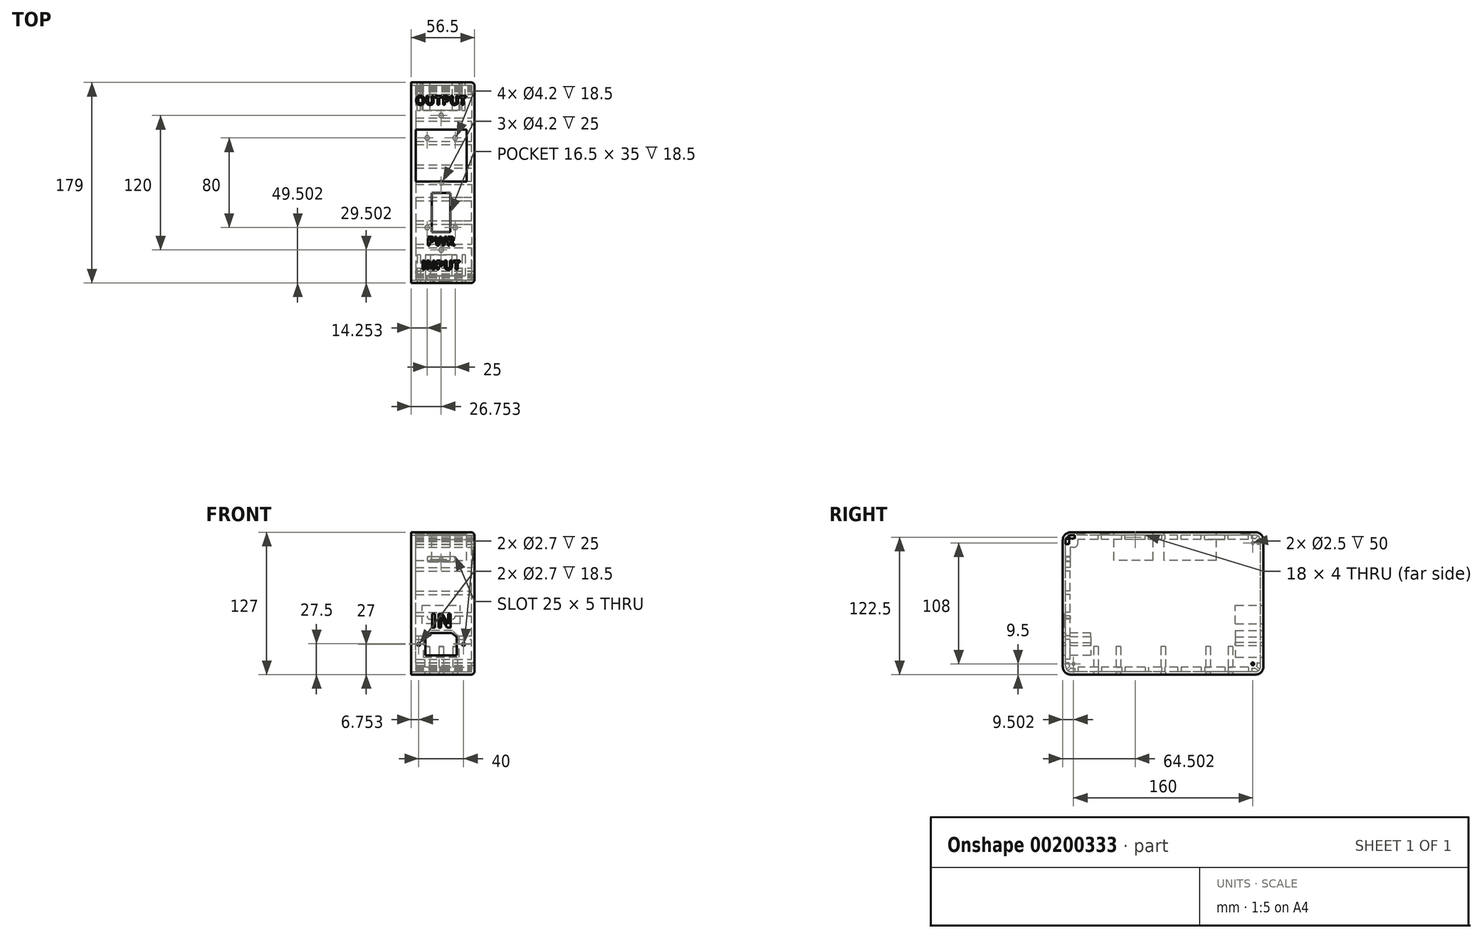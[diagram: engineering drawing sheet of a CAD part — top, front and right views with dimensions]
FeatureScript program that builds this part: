
annotation { "Feature Type Name" : "Feature", "Feature Type Description" : "" }
export const myFeature = defineFeature(function(context is Context, id is Id, definition is map)
    precondition{}
    {
        {
            var Q0;
            Q0=qCreatedBy(makeId("Top.planeOp"),FACE);
            var sketch = newSketch(context, id + "F0", { "sketchPlane" : qUnion([Q0])});
            skLineSegment(sketch, "E0.bottom", {"start": v(-53, 83.4) * mm, "end": v(59, 83.4) * mm});
            skLineSegment(sketch, "E0.top", {"start": v(-53, -90.6) * mm, "end": v(59, -90.6) * mm});
            skLineSegment(sketch, "E0.left", {"start": v(-58, 78.4) * mm, "end": v(-58, -85.6) * mm});
            skLineSegment(sketch, "E0.right", {"start": v(64, 78.4) * mm, "end": v(64, -85.6) * mm});
            skLineSegment(sketch, "E1.1", {"start": v(-54, 72.4) * mm, "end": v(-54, -79.6) * mm});
            skLineSegment(sketch, "E1.2", {"start": v(-47, -86.6) * mm, "end": v(53, -86.6) * mm});
            skLineSegment(sketch, "E1.3", {"start": v(60, 72.4) * mm, "end": v(60, -79.6) * mm});
            skLineSegment(sketch, "E2.bottom", {"start": v(-29, 49.4) * mm, "end": v(16, 49.4) * mm, "construction": true});
            skLineSegment(sketch, "E2.top", {"start": v(-29, 3.4) * mm, "end": v(16, 3.4) * mm, "construction": true});
            skLineSegment(sketch, "E2.left", {"start": v(-29, 49.4) * mm, "end": v(-29, 3.4) * mm, "construction": true});
            skLineSegment(sketch, "E2.right", {"start": v(16, 49.4) * mm, "end": v(16, 3.4) * mm, "construction": true});
            skLineSegment(sketch, "E3.0", {"start": v(-60.5, 78.9) * mm, "end": v(-60.5, -86.1) * mm});
            skLineSegment(sketch, "E3.1", {"start": v(-53.5, 85.9) * mm, "end": v(59.5, 85.9) * mm});
            skLineSegment(sketch, "E3.2", {"start": v(66.5, 78.9) * mm, "end": v(66.5, -86.1) * mm});
            skLineSegment(sketch, "E3.3", {"start": v(-53.5, -93.1) * mm, "end": v(59.5, -93.1) * mm});
            skLineSegment(sketch, "E4", {"start": v(66, 49.4) * mm, "end": v(98.5, 49.4) * mm, "construction": true});
            skLineSegment(sketch, "E5", {"start": v(98.5, 49.4) * mm, "end": v(98.5, 32.4) * mm, "construction": true});
            skLineSegment(sketch, "E6", {"start": v(98.5, 32.4) * mm, "end": v(92.24, 25.4) * mm, "construction": true});
            skLineSegment(sketch, "E7", {"start": v(92.24, 25.4) * mm, "end": v(72.24, 25.4) * mm, "construction": true});
            skLineSegment(sketch, "E8", {"start": v(72.24, 25.4) * mm, "end": v(66, 32.4) * mm, "construction": true});
            skLineSegment(sketch, "E9", {"start": v(66, 32.4) * mm, "end": v(66, 49.4) * mm, "construction": true});
            skLineSegment(sketch, "E10", {"start": v(82.24, 25.4) * mm, "end": v(82.24, 49.4) * mm, "construction": true});
            skLineSegment(sketch, "E11.bottom", {"start": v(65.5, 3.4) * mm, "end": v(99, 3.4) * mm, "construction": true});
            skLineSegment(sketch, "E11.top", {"start": v(65.5, 19.4) * mm, "end": v(99, 19.4) * mm, "construction": true});
            skLineSegment(sketch, "E11.left", {"start": v(65.5, 3.4) * mm, "end": v(65.5, 19.4) * mm, "construction": true});
            skLineSegment(sketch, "E11.right", {"start": v(99, 3.4) * mm, "end": v(99, 19.4) * mm, "construction": true});
            skLineSegment(sketch, "E12", {"start": v(82.24, 19.4) * mm, "end": v(82.24, 25.4) * mm, "construction": true});
            skLineSegment(sketch, "E13.bottom", {"start": v(26, 9.4) * mm, "end": v(41, 9.4) * mm, "construction": true});
            skLineSegment(sketch, "E13.top", {"start": v(26, 43.4) * mm, "end": v(41, 43.4) * mm, "construction": true});
            skLineSegment(sketch, "E13.left", {"start": v(26, 9.4) * mm, "end": v(26, 43.4) * mm, "construction": true});
            skLineSegment(sketch, "E13.right", {"start": v(41, 9.4) * mm, "end": v(41, 43.4) * mm, "construction": true});
            skLineSegment(sketch, "E14", {"start": v(26, 26.4) * mm, "end": v(16, 26.4) * mm, "construction": true});
            skPoint(sketch, "E15.visualSharp", {"position": v(-54, 79.4) * mm});
            skArc(sketch, "E15.filletArc", {"start": v(-51, 79.28) * mm, "mid": v(-52.84, 78.23) * mm, "end": v(-53.88, 76.4) * mm});
            skPoint(sketch, "E16.visualSharp", {"position": v(60, 79.4) * mm});
            skPoint(sketch, "E17.visualSharp", {"position": v(-54, -86.6) * mm});
            skArc(sketch, "E17.filletArc", {"start": v(-53.88, -83.6) * mm, "mid": v(-52.84, -85.43) * mm, "end": v(-51, -86.47) * mm});
            skPoint(sketch, "E18.visualSharp", {"position": v(60, -86.6) * mm});
            skPoint(sketch, "E19.visualSharp", {"position": v(64, -90.6) * mm});
            skArc(sketch, "E19.filletArc", {"start": v(59, -90.6) * mm, "mid": v(62.53, -89.13) * mm, "end": v(64, -85.6) * mm});
            skPoint(sketch, "E20.visualSharp", {"position": v(-58, -90.6) * mm});
            skArc(sketch, "E20.filletArc", {"start": v(-58, -85.6) * mm, "mid": v(-56.54, -89.13) * mm, "end": v(-53, -90.6) * mm});
            skPoint(sketch, "E21.visualSharp", {"position": v(64, 83.4) * mm});
            skArc(sketch, "E21.filletArc", {"start": v(64, 78.4) * mm, "mid": v(62.53, 81.94) * mm, "end": v(59, 83.4) * mm});
            skPoint(sketch, "E22.visualSharp", {"position": v(-58, 83.4) * mm});
            skArc(sketch, "E22.filletArc", {"start": v(-53, 83.4) * mm, "mid": v(-56.54, 81.94) * mm, "end": v(-58, 78.4) * mm});
            skPoint(sketch, "E23.visualSharp", {"position": v(-60.5, 85.9) * mm});
            skArc(sketch, "E23.filletArc", {"start": v(-53.5, 85.9) * mm, "mid": v(-58.46, 83.85) * mm, "end": v(-60.5, 78.9) * mm});
            skPoint(sketch, "E24.visualSharp", {"position": v(66.5, 85.9) * mm});
            skArc(sketch, "E24.filletArc", {"start": v(66.5, 78.9) * mm, "mid": v(64.44, 83.85) * mm, "end": v(59.5, 85.9) * mm});
            skPoint(sketch, "E25.visualSharp", {"position": v(66.5, -93.1) * mm});
            skArc(sketch, "E25.filletArc", {"start": v(59.5, -93.1) * mm, "mid": v(64.44, -91.05) * mm, "end": v(66.5, -86.1) * mm});
            skPoint(sketch, "E26.visualSharp", {"position": v(-60.5, -93.1) * mm});
            skArc(sketch, "E26.filletArc", {"start": v(-60.5, -86.1) * mm, "mid": v(-58.46, -91.05) * mm, "end": v(-53.5, -93.1) * mm});
            skLineSegment(sketch, "E27", {"start": v(-50, 80.28) * mm, "end": v(-50, 83.4) * mm});
            skLineSegment(sketch, "E28", {"start": v(-52.95, 78.1) * mm, "end": v(-56.54, 81.94) * mm, "construction": true});
            skLineSegment(sketch, "E29.0", {"start": v(-53.15, 79.78) * mm, "end": v(-55.77, 82.57) * mm});
            skLineSegment(sketch, "E30.0", {"start": v(-54.52, 78.32) * mm, "end": v(-57.18, 81.16) * mm});
            skLineSegment(sketch, "E31.0", {"start": v(-47, 76.4) * mm, "end": v(-47, 83.4) * mm});
            skLineSegment(sketch, "E32.0", {"start": v(-29, 79.4) * mm, "end": v(-29, 83.4) * mm});
            skLineSegment(sketch, "E33.0", {"start": v(-26, 79.4) * mm, "end": v(-26, 83.4) * mm});
            skLineSegment(sketch, "E34.0", {"start": v(-8, 79.4) * mm, "end": v(-8, 83.4) * mm});
            skLineSegment(sketch, "E35.0", {"start": v(-5, 79.4) * mm, "end": v(-5, 83.4) * mm});
            skLineSegment(sketch, "E36", {"start": v(3, 85.9) * mm, "end": v(3, 79.4) * mm, "construction": true});
            skLineSegment(sketch, "E37", {"start": v(-54.88, 75.4) * mm, "end": v(-58, 75.4) * mm});
            skLineSegment(sketch, "E38.0", {"start": v(-51, 72.4) * mm, "end": v(-58, 72.4) * mm});
            skLineSegment(sketch, "E39.0", {"start": v(-54, 54.4) * mm, "end": v(-58, 54.4) * mm});
            skLineSegment(sketch, "E40.0", {"start": v(-54, 51.4) * mm, "end": v(-58, 51.4) * mm});
            skLineSegment(sketch, "E41.0", {"start": v(-54, 33.4) * mm, "end": v(-58, 33.4) * mm});
            skLineSegment(sketch, "E42.0", {"start": v(-54, 30.4) * mm, "end": v(-58, 30.4) * mm});
            skLineSegment(sketch, "E43.0", {"start": v(-54, 12.4) * mm, "end": v(-58, 12.4) * mm});
            skLineSegment(sketch, "E44.0", {"start": v(-54, 9.4) * mm, "end": v(-58, 9.4) * mm});
            skLineSegment(sketch, "E45", {"start": v(-60.5, -3.6) * mm, "end": v(-54, -3.6) * mm, "construction": true});
            skLineSegment(sketch, "E46.0", {"start": v(-58, -2.1) * mm, "end": v(-54, -2.1) * mm});
            skLineSegment(sketch, "E47.MirrorCS", {"start": v(-58, -5.1) * mm, "end": v(-54, -5.1) * mm});
            skLineSegment(sketch, "E48.MirrorCS", {"start": v(-54, -16.6) * mm, "end": v(-58, -16.6) * mm});
            skLineSegment(sketch, "E49.MirrorCS", {"start": v(-54, -19.6) * mm, "end": v(-58, -19.6) * mm});
            skLineSegment(sketch, "E50.MirrorCS", {"start": v(-54, -37.6) * mm, "end": v(-58, -37.6) * mm});
            skLineSegment(sketch, "E51.MirrorCS", {"start": v(-54, -40.6) * mm, "end": v(-58, -40.6) * mm});
            skLineSegment(sketch, "E52.MirrorCS", {"start": v(-51, -79.6) * mm, "end": v(-58, -79.6) * mm});
            skLineSegment(sketch, "E53.MirrorCS", {"start": v(-54.88, -82.6) * mm, "end": v(-58, -82.6) * mm});
            skLineSegment(sketch, "E54.MirrorCS", {"start": v(-54.52, -85.51) * mm, "end": v(-57.18, -88.35) * mm});
            skLineSegment(sketch, "E55.MirrorCS", {"start": v(-53.15, -86.98) * mm, "end": v(-55.77, -89.77) * mm});
            skLineSegment(sketch, "E56.MirrorCS", {"start": v(-50, -87.47) * mm, "end": v(-50, -90.6) * mm});
            skLineSegment(sketch, "E57.MirrorCS", {"start": v(-47, -83.6) * mm, "end": v(-47, -90.6) * mm});
            skLineSegment(sketch, "E58.MirrorCS", {"start": v(-29, -86.6) * mm, "end": v(-29, -90.6) * mm});
            skLineSegment(sketch, "E59.MirrorCS", {"start": v(-26, -86.6) * mm, "end": v(-26, -90.6) * mm});
            skLineSegment(sketch, "E60.MirrorCS", {"start": v(-8, -86.6) * mm, "end": v(-8, -90.6) * mm});
            skLineSegment(sketch, "E61.MirrorCS", {"start": v(-5, -86.6) * mm, "end": v(-5, -90.6) * mm});
            skLineSegment(sketch, "E62.MirrorCS", {"start": v(-54, -61.6) * mm, "end": v(-58, -61.6) * mm});
            skLineSegment(sketch, "E63.MirrorCS", {"start": v(-54, -58.6) * mm, "end": v(-58, -58.6) * mm});
            skLineSegment(sketch, "E64.MirrorCS", {"start": v(11, 79.4) * mm, "end": v(11, 83.4) * mm});
            skLineSegment(sketch, "E65.MirrorCS", {"start": v(14, 79.4) * mm, "end": v(14, 83.4) * mm});
            skLineSegment(sketch, "E66.MirrorCS", {"start": v(32, 79.4) * mm, "end": v(32, 83.4) * mm});
            skLineSegment(sketch, "E67.MirrorCS", {"start": v(35, 79.4) * mm, "end": v(35, 83.4) * mm});
            skLineSegment(sketch, "E68.MirrorCS", {"start": v(53, 76.4) * mm, "end": v(53, 83.4) * mm});
            skLineSegment(sketch, "E69.MirrorCS", {"start": v(56, 79.4) * mm, "end": v(56, 83.4) * mm});
            skLineSegment(sketch, "E70.MirrorCS", {"start": v(59.13, 79.78) * mm, "end": v(61.75, 82.57) * mm});
            skLineSegment(sketch, "E71.MirrorCS", {"start": v(60.5, 78.32) * mm, "end": v(63.17, 81.16) * mm});
            skLineSegment(sketch, "E72.MirrorCS", {"start": v(60, 75.4) * mm, "end": v(64, 75.4) * mm});
            skLineSegment(sketch, "E73.MirrorCS", {"start": v(57, 72.4) * mm, "end": v(64, 72.4) * mm});
            skLineSegment(sketch, "E74.MirrorCS", {"start": v(60, 54.4) * mm, "end": v(64, 54.4) * mm});
            skLineSegment(sketch, "E75.MirrorCS", {"start": v(60, 51.4) * mm, "end": v(64, 51.4) * mm});
            skLineSegment(sketch, "E76.MirrorCS", {"start": v(60, 33.4) * mm, "end": v(64, 33.4) * mm});
            skLineSegment(sketch, "E77.MirrorCS", {"start": v(60, 30.4) * mm, "end": v(64, 30.4) * mm});
            skLineSegment(sketch, "E78.MirrorCS", {"start": v(60, 12.4) * mm, "end": v(64, 12.4) * mm});
            skLineSegment(sketch, "E79.MirrorCS", {"start": v(60, 9.4) * mm, "end": v(64, 9.4) * mm});
            skLineSegment(sketch, "E80.MirrorCS", {"start": v(64, -2.1) * mm, "end": v(60, -2.1) * mm});
            skLineSegment(sketch, "E81.MirrorCS", {"start": v(64, -5.1) * mm, "end": v(60, -5.1) * mm});
            skLineSegment(sketch, "E82.MirrorCS", {"start": v(60, -16.6) * mm, "end": v(64, -16.6) * mm});
            skLineSegment(sketch, "E83.MirrorCS", {"start": v(60, -19.6) * mm, "end": v(64, -19.6) * mm});
            skLineSegment(sketch, "E84.MirrorCS", {"start": v(60, -37.6) * mm, "end": v(64, -37.6) * mm});
            skLineSegment(sketch, "E85.MirrorCS", {"start": v(60, -40.6) * mm, "end": v(64, -40.6) * mm});
            skLineSegment(sketch, "E86.MirrorCS", {"start": v(60, -58.6) * mm, "end": v(64, -58.6) * mm});
            skLineSegment(sketch, "E87.MirrorCS", {"start": v(60, -61.6) * mm, "end": v(64, -61.6) * mm});
            skLineSegment(sketch, "E88.MirrorCS", {"start": v(57, -79.6) * mm, "end": v(64, -79.6) * mm});
            skLineSegment(sketch, "E89.MirrorCS", {"start": v(60, -82.6) * mm, "end": v(64, -82.6) * mm});
            skLineSegment(sketch, "E90.MirrorCS", {"start": v(11, -86.6) * mm, "end": v(11, -90.6) * mm});
            skLineSegment(sketch, "E91.MirrorCS", {"start": v(14, -86.6) * mm, "end": v(14, -90.6) * mm});
            skLineSegment(sketch, "E92.MirrorCS", {"start": v(32, -86.6) * mm, "end": v(32, -90.6) * mm});
            skLineSegment(sketch, "E93.MirrorCS", {"start": v(35, -86.6) * mm, "end": v(35, -90.6) * mm});
            skLineSegment(sketch, "E94.MirrorCS", {"start": v(53, -83.6) * mm, "end": v(53, -90.6) * mm});
            skLineSegment(sketch, "E95.MirrorCS", {"start": v(56, -86.6) * mm, "end": v(56, -90.6) * mm});
            skLineSegment(sketch, "E96.MirrorCS", {"start": v(59.53, -84.47) * mm, "end": v(63.17, -88.35) * mm});
            skLineSegment(sketch, "E97.MirrorCS", {"start": v(58.17, -85.95) * mm, "end": v(61.75, -89.77) * mm});
            skLineSegment(sketch, "E98", {"start": v(-60.5, -83.6) * mm, "end": v(66.5, -83.6) * mm, "construction": true});
            skLineSegment(sketch, "E99", {"start": v(-51, 85.9) * mm, "end": v(-51, -93.1) * mm, "construction": true});
            skLineSegment(sketch, "E100", {"start": v(57, -93.1) * mm, "end": v(57, 85.9) * mm, "construction": true});
            skLineSegment(sketch, "E101", {"start": v(-60.5, 76.4) * mm, "end": v(66.5, 76.4) * mm, "construction": true});
            skArc(sketch, "E102", {"start": v(-53.15, -86.98) * mm, "mid": v(-51.63, -87.55) * mm, "end": v(-50, -87.47) * mm});
            skCircle(sketch, "E103", {"center": v(-51, -83.6) * mm, "radius": 1.25 * mm});
            skPoint(sketch, "E104.orphan", {"position": v(-52.19, -85.95) * mm});
            skPoint(sketch, "E105.orphan", {"position": v(-53.54, -84.47) * mm});
            skArc(sketch, "E106.trimOffspring", {"start": v(-48.36, -86.6) * mm, "mid": v(-48.18, -80.77) * mm, "end": v(-54, -80.95) * mm});
            skPoint(sketch, "E107.orphan", {"position": v(-50, -86.6) * mm});
            skPoint(sketch, "E108.orphan", {"position": v(-54, -82.6) * mm});
            skArc(sketch, "E109.trimOffspring", {"start": v(-54.88, -82.6) * mm, "mid": v(-54.98, -84.1) * mm, "end": v(-54.52, -85.51) * mm});
            skLineSegment(sketch, "E110.trimOffspring", {"start": v(-54, -80.95) * mm, "end": v(-54, -82.6) * mm});
            skArc(sketch, "E111.MirrorCS", {"start": v(-47, 76.4) * mm, "mid": v(-48.18, 73.57) * mm, "end": v(-51, 72.4) * mm});
            skCircle(sketch, "E112.MirrorC", {"center": v(-51, 76.4) * mm, "radius": 1.25 * mm});
            skArc(sketch, "E113.MirrorCS", {"start": v(-54.88, 75.4) * mm, "mid": v(-54.98, 76.9) * mm, "end": v(-54.52, 78.32) * mm});
            skArc(sketch, "E114.MirrorCS", {"start": v(-53.15, 79.78) * mm, "mid": v(-51.63, 80.35) * mm, "end": v(-50, 80.28) * mm});
            skPoint(sketch, "E115.orphan", {"position": v(-52.19, 78.76) * mm});
            skPoint(sketch, "E116.orphan", {"position": v(-53.54, 77.28) * mm});
            skLineSegment(sketch, "E117.trimOffspring", {"start": v(-29, 79.4) * mm, "end": v(-26, 79.4) * mm});
            skPoint(sketch, "E1.0.end.orphan", {"position": v(-48.36, 79.4) * mm});
            skPoint(sketch, "E1.0.start.orphan", {"position": v(-50, 79.4) * mm});
            skPoint(sketch, "E118.orphan", {"position": v(-54, 75.4) * mm});
            skPoint(sketch, "E119.orphan", {"position": v(-54, 73.76) * mm});
            skLineSegment(sketch, "E120.trimOffspring", {"start": v(-8, 79.4) * mm, "end": v(-5, 79.4) * mm});
            skLineSegment(sketch, "E121.trimOffspring", {"start": v(11, 79.4) * mm, "end": v(14, 79.4) * mm});
            skLineSegment(sketch, "E122.trimOffspring", {"start": v(32, 79.4) * mm, "end": v(35, 79.4) * mm});
            skArc(sketch, "E123.MirrorCS", {"start": v(53, 76.4) * mm, "mid": v(54.16, 73.57) * mm, "end": v(57, 72.4) * mm});
            skCircle(sketch, "E124.MirrorC", {"center": v(57, 76.4) * mm, "radius": 1.25 * mm});
            skArc(sketch, "E125.MirrorCS", {"start": v(59.13, 79.78) * mm, "mid": v(57.61, 80.35) * mm, "end": v(56, 80.28) * mm});
            skArc(sketch, "E126.MirrorCS", {"start": v(60.87, 75.4) * mm, "mid": v(60.96, 76.9) * mm, "end": v(60.5, 78.32) * mm});
            skArc(sketch, "E127.MirrorCS", {"start": v(53, -83.6) * mm, "mid": v(54.16, -80.77) * mm, "end": v(57, -79.6) * mm});
            skArc(sketch, "E128.MirrorCS", {"start": v(59.13, -86.98) * mm, "mid": v(57.61, -87.55) * mm, "end": v(56, -87.47) * mm});
            skArc(sketch, "E129.MirrorCS", {"start": v(60.87, -82.6) * mm, "mid": v(60.96, -84.1) * mm, "end": v(60.5, -85.51) * mm});
            skCircle(sketch, "E130", {"center": v(57, -83.6) * mm, "radius": 1.25 * mm});
            skPoint(sketch, "E131.orphan", {"position": v(54.35, -86.6) * mm});
            skPoint(sketch, "E132.orphan", {"position": v(60, -80.95) * mm});
            skLineSegment(sketch, "E133.trimOffspring", {"start": v(54.35, -86.6) * mm, "end": v(56, -86.6) * mm});
            skPoint(sketch, "E134.orphan", {"position": v(59.53, 77.28) * mm});
            skPoint(sketch, "E135.orphan", {"position": v(58.17, 78.76) * mm});
            skPoint(sketch, "E136.orphan", {"position": v(-60.5, -2.1) * mm});
            skPoint(sketch, "E137.orphan", {"position": v(-60.5, -5.1) * mm});
            skPoint(sketch, "E138.orphan", {"position": v(66.5, -2.1) * mm});
            skPoint(sketch, "E139.orphan", {"position": v(66.5, -5.1) * mm});
            skSolve(sketch);
        }
        {
            var Q0;
            Q0=makeQuery(id+"F0.imprint","IMPRINT",FACE,{"disambiguationData":[TD([[makeQuery(id+"F0.imprint","IMPRINT",EDGE,{"derivedFrom":sQuery(id+"F0.wireOp",EDGE,"E3.1")}),-1.0]])]});
            extrude(context, id + "F1", {"entities" : qUnion([Q0]), "depth" : 56.5 * mm});
        }
        {
            var Q0;
            {var subQ8=sQuery(id+"F0.wireOp",EDGE,"E32.0");Q0=makeQuery(id+"F0.imprint","IMPRINT",FACE,{"disambiguationData":[TD([[makeQuery(id+"F0.imprint","IMPRINT",EDGE,{"derivedFrom":subQ8}),1.0]])]});}
            var Q1;
            {var subQ1=sQuery(id+"F0.wireOp",EDGE,"E27");Q1=makeQuery(id+"F0.imprint","IMPRINT",FACE,{"disambiguationData":[TD([[makeQuery(id+"F0.imprint","IMPRINT",EDGE,{"derivedFrom":subQ1}),1.0]])]});}
            var Q2;
            {var subQ1=sQuery(id+"F0.wireOp",EDGE,"E30.0");Q2=makeQuery(id+"F0.imprint","IMPRINT",FACE,{"disambiguationData":[TD([[makeQuery(id+"F0.imprint","IMPRINT",EDGE,{"derivedFrom":subQ1}),1.0]])]});}
            var Q3;
            {var subQ0=sQuery(id+"F0.wireOp",EDGE,"E39.0");Q3=makeQuery(id+"F0.imprint","IMPRINT",FACE,{"disambiguationData":[TD([[makeQuery(id+"F0.imprint","IMPRINT",EDGE,{"derivedFrom":subQ0}),-1.0]])]});}
            var Q4;
            {var subQ0=sQuery(id+"F0.wireOp",EDGE,"E40.0");Q4=makeQuery(id+"F0.imprint","IMPRINT",FACE,{"disambiguationData":[TD([[makeQuery(id+"F0.imprint","IMPRINT",EDGE,{"derivedFrom":subQ0}),1.0]])]});}
            var Q5;
            {var subQ0=sQuery(id+"F0.wireOp",EDGE,"E42.0");Q5=makeQuery(id+"F0.imprint","IMPRINT",FACE,{"disambiguationData":[TD([[makeQuery(id+"F0.imprint","IMPRINT",EDGE,{"derivedFrom":subQ0}),1.0]])]});}
            var Q6;
            {var subQ0=sQuery(id+"F0.wireOp",EDGE,"E74.MirrorCS");Q6=makeQuery(id+"F0.imprint","IMPRINT",FACE,{"disambiguationData":[TD([[makeQuery(id+"F0.imprint","IMPRINT",EDGE,{"derivedFrom":subQ0}),1.0]])]});}
            var Q7;
            {var subQ0=sQuery(id+"F0.wireOp",EDGE,"E75.MirrorCS");Q7=makeQuery(id+"F0.imprint","IMPRINT",FACE,{"disambiguationData":[TD([[makeQuery(id+"F0.imprint","IMPRINT",EDGE,{"derivedFrom":subQ0}),-1.0]])]});}
            var Q8;
            {var subQ4=sQuery(id+"F0.wireOp",EDGE,"E71.MirrorCS");Q8=makeQuery(id+"F0.imprint","IMPRINT",FACE,{"disambiguationData":[TD([[makeQuery(id+"F0.imprint","IMPRINT",EDGE,{"derivedFrom":subQ4}),-1.0]])]});}
            var Q9;
            {var subQ6=sQuery(id+"F0.wireOp",EDGE,"E70.MirrorCS");Q9=makeQuery(id+"F0.imprint","IMPRINT",FACE,{"disambiguationData":[TD([[makeQuery(id+"F0.imprint","IMPRINT",EDGE,{"derivedFrom":subQ6}),1.0]])]});}
            var Q10;
            {var subQ0=sQuery(id+"F0.wireOp",EDGE,"E77.MirrorCS");Q10=makeQuery(id+"F0.imprint","IMPRINT",FACE,{"disambiguationData":[TD([[makeQuery(id+"F0.imprint","IMPRINT",EDGE,{"derivedFrom":subQ0}),-1.0]])]});}
            var Q11;
            {var subQ0=sQuery(id+"F0.wireOp",EDGE,"E79.MirrorCS");Q11=makeQuery(id+"F0.imprint","IMPRINT",FACE,{"disambiguationData":[TD([[makeQuery(id+"F0.imprint","IMPRINT",EDGE,{"derivedFrom":subQ0}),-1.0]])]});}
            var Q12;
            {var subQ0=sQuery(id+"F0.wireOp",EDGE,"E81.MirrorCS");Q12=makeQuery(id+"F0.imprint","IMPRINT",FACE,{"disambiguationData":[TD([[makeQuery(id+"F0.imprint","IMPRINT",EDGE,{"derivedFrom":subQ0}),1.0]])]});}
            var Q13;
            {var subQ0=sQuery(id+"F0.wireOp",EDGE,"E83.MirrorCS");Q13=makeQuery(id+"F0.imprint","IMPRINT",FACE,{"disambiguationData":[TD([[makeQuery(id+"F0.imprint","IMPRINT",EDGE,{"derivedFrom":subQ0}),-1.0]])]});}
            var Q14;
            {var subQ0=sQuery(id+"F0.wireOp",EDGE,"E85.MirrorCS");Q14=makeQuery(id+"F0.imprint","IMPRINT",FACE,{"disambiguationData":[TD([[makeQuery(id+"F0.imprint","IMPRINT",EDGE,{"derivedFrom":subQ0}),-1.0]])]});}
            var Q15;
            {var subQ0=sQuery(id+"F0.wireOp",EDGE,"E87.MirrorCS");Q15=makeQuery(id+"F0.imprint","IMPRINT",FACE,{"disambiguationData":[TD([[makeQuery(id+"F0.imprint","IMPRINT",EDGE,{"derivedFrom":subQ0}),-1.0]])]});}
            var Q16;
            {var subQ0=sQuery(id+"F0.wireOp",EDGE,"E44.0");Q16=makeQuery(id+"F0.imprint","IMPRINT",FACE,{"disambiguationData":[TD([[makeQuery(id+"F0.imprint","IMPRINT",EDGE,{"derivedFrom":subQ0}),1.0]])]});}
            var Q17;
            {var subQ0=sQuery(id+"F0.wireOp",EDGE,"E47.MirrorCS");Q17=makeQuery(id+"F0.imprint","IMPRINT",FACE,{"disambiguationData":[TD([[makeQuery(id+"F0.imprint","IMPRINT",EDGE,{"derivedFrom":subQ0}),-1.0]])]});}
            var Q18;
            {var subQ0=sQuery(id+"F0.wireOp",EDGE,"E49.MirrorCS");Q18=makeQuery(id+"F0.imprint","IMPRINT",FACE,{"disambiguationData":[TD([[makeQuery(id+"F0.imprint","IMPRINT",EDGE,{"derivedFrom":subQ0}),1.0]])]});}
            var Q19;
            {var subQ0=sQuery(id+"F0.wireOp",EDGE,"E51.MirrorCS");Q19=makeQuery(id+"F0.imprint","IMPRINT",FACE,{"disambiguationData":[TD([[makeQuery(id+"F0.imprint","IMPRINT",EDGE,{"derivedFrom":subQ0}),1.0]])]});}
            var Q20;
            {var subQ3=sQuery(id+"F0.wireOp",EDGE,"E62.MirrorCS");Q20=makeQuery(id+"F0.imprint","IMPRINT",FACE,{"disambiguationData":[TD([[makeQuery(id+"F0.imprint","IMPRINT",EDGE,{"derivedFrom":subQ3}),1.0]])]});}
            var Q21;
            {var subQ1=sQuery(id+"F0.wireOp",EDGE,"E53.MirrorCS");Q21=makeQuery(id+"F0.imprint","IMPRINT",FACE,{"disambiguationData":[TD([[makeQuery(id+"F0.imprint","IMPRINT",EDGE,{"derivedFrom":subQ1}),1.0]])]});}
            var Q22;
            {var subQ0=sQuery(id+"F0.wireOp",EDGE,"E55.MirrorCS");Q22=makeQuery(id+"F0.imprint","IMPRINT",FACE,{"disambiguationData":[TD([[makeQuery(id+"F0.imprint","IMPRINT",EDGE,{"derivedFrom":subQ0}),1.0]])]});}
            var Q23;
            {var subQ3=sQuery(id+"F0.wireOp",EDGE,"E58.MirrorCS");Q23=makeQuery(id+"F0.imprint","IMPRINT",FACE,{"disambiguationData":[TD([[makeQuery(id+"F0.imprint","IMPRINT",EDGE,{"derivedFrom":subQ3}),-1.0]])]});}
            var Q24;
            {var subQ0=sQuery(id+"F0.wireOp",EDGE,"E59.MirrorCS");Q24=makeQuery(id+"F0.imprint","IMPRINT",FACE,{"disambiguationData":[TD([[makeQuery(id+"F0.imprint","IMPRINT",EDGE,{"derivedFrom":subQ0}),1.0]])]});}
            var Q25;
            {var subQ0=sQuery(id+"F0.wireOp",EDGE,"E61.MirrorCS");Q25=makeQuery(id+"F0.imprint","IMPRINT",FACE,{"disambiguationData":[TD([[makeQuery(id+"F0.imprint","IMPRINT",EDGE,{"derivedFrom":subQ0}),1.0]])]});}
            var Q26;
            {var subQ0=sQuery(id+"F0.wireOp",EDGE,"E91.MirrorCS");Q26=makeQuery(id+"F0.imprint","IMPRINT",FACE,{"disambiguationData":[TD([[makeQuery(id+"F0.imprint","IMPRINT",EDGE,{"derivedFrom":subQ0}),1.0]])]});}
            var Q27;
            {var subQ0=sQuery(id+"F0.wireOp",EDGE,"E93.MirrorCS");Q27=makeQuery(id+"F0.imprint","IMPRINT",FACE,{"disambiguationData":[TD([[makeQuery(id+"F0.imprint","IMPRINT",EDGE,{"derivedFrom":subQ0}),1.0]])]});}
            var Q28;
            {var subQ3=sQuery(id+"F0.wireOp",EDGE,"E128.MirrorCS");Q28=makeQuery(id+"F0.imprint","IMPRINT",FACE,{"disambiguationData":[TD([[makeQuery(id+"F0.imprint","IMPRINT",EDGE,{"derivedFrom":subQ3}),1.0]])]});}
            var Q29;
            {var subQ3=sQuery(id+"F0.wireOp",EDGE,"E129.MirrorCS");Q29=makeQuery(id+"F0.imprint","IMPRINT",FACE,{"disambiguationData":[TD([[makeQuery(id+"F0.imprint","IMPRINT",EDGE,{"derivedFrom":subQ3}),1.0]])]});}
            var Q30;
            Q30=makeQuery(id+"F0.imprint","IMPRINT",FACE,{"disambiguationData":[TD([[makeQuery(id+"F0.imprint","IMPRINT",EDGE,{"derivedFrom":sQuery(id+"F0.wireOp",EDGE,"E130")}),1.0]])]});
            var Q31;
            Q31=makeQuery(id+"F0.imprint","IMPRINT",FACE,{"disambiguationData":[TD([[makeQuery(id+"F0.imprint","IMPRINT",EDGE,{"derivedFrom":sQuery(id+"F0.wireOp",EDGE,"E103")}),1.0]])]});
            var Q32;
            Q32=makeQuery(id+"F0.imprint","IMPRINT",FACE,{"disambiguationData":[TD([[makeQuery(id+"F0.imprint","IMPRINT",EDGE,{"derivedFrom":sQuery(id+"F0.wireOp",EDGE,"E112.MirrorC")}),-1.0]])]});
            var Q33;
            Q33=makeQuery(id+"F0.imprint","IMPRINT",FACE,{"disambiguationData":[TD([[makeQuery(id+"F0.imprint","IMPRINT",EDGE,{"derivedFrom":sQuery(id+"F0.wireOp",EDGE,"E124.MirrorC")}),1.0]])]});
            extrude(context, id + "F2", {"entities" : qUnion([Q0, Q1, Q2, Q3, Q4, Q5, Q6, Q7, Q8, Q9, Q10, Q11, Q12, Q13, Q14, Q15, Q16, Q17, Q18, Q19, Q20, Q21, Q22, Q23, Q24, Q25, Q26, Q27, Q28, Q29, Q30, Q31, Q32, Q33]), "operationType" : NewBodyOperationType.ADD, "depth" : 2.5 * mm});
        }
        {
            var Q0;
            {var subQ9=sQuery(id+"F0.wireOp",EDGE,"E27");Q0=makeQuery(id+"F0.imprint","IMPRINT",FACE,{"disambiguationData":[TD([[makeQuery(id+"F0.imprint","IMPRINT",EDGE,{"derivedFrom":subQ9}),-1.0]])]});}
            var Q1;
            {var subQ0=sQuery(id+"F0.wireOp",EDGE,"E32.0");Q1=makeQuery(id+"F0.imprint","IMPRINT",FACE,{"disambiguationData":[TD([[makeQuery(id+"F0.imprint","IMPRINT",EDGE,{"derivedFrom":subQ0}),-1.0]])]});}
            var Q2;
            {var subQ0=sQuery(id+"F0.wireOp",EDGE,"E34.0");Q2=makeQuery(id+"F0.imprint","IMPRINT",FACE,{"disambiguationData":[TD([[makeQuery(id+"F0.imprint","IMPRINT",EDGE,{"derivedFrom":subQ0}),-1.0]])]});}
            var Q3;
            {var subQ0=sQuery(id+"F0.wireOp",EDGE,"E39.0");Q3=makeQuery(id+"F0.imprint","IMPRINT",FACE,{"disambiguationData":[TD([[makeQuery(id+"F0.imprint","IMPRINT",EDGE,{"derivedFrom":subQ0}),1.0]])]});}
            var Q4;
            {var subQ0=sQuery(id+"F0.wireOp",EDGE,"E64.MirrorCS");Q4=makeQuery(id+"F0.imprint","IMPRINT",FACE,{"disambiguationData":[TD([[makeQuery(id+"F0.imprint","IMPRINT",EDGE,{"derivedFrom":subQ0}),-1.0]])]});}
            var Q5;
            {var subQ0=sQuery(id+"F0.wireOp",EDGE,"E66.MirrorCS");Q5=makeQuery(id+"F0.imprint","IMPRINT",FACE,{"disambiguationData":[TD([[makeQuery(id+"F0.imprint","IMPRINT",EDGE,{"derivedFrom":subQ0}),-1.0]])]});}
            var Q6;
            {var subQ8=sQuery(id+"F0.wireOp",EDGE,"E70.MirrorCS");Q6=makeQuery(id+"F0.imprint","IMPRINT",FACE,{"disambiguationData":[TD([[makeQuery(id+"F0.imprint","IMPRINT",EDGE,{"derivedFrom":subQ8}),-1.0]])]});}
            var Q7;
            {var subQ0=sQuery(id+"F0.wireOp",EDGE,"E74.MirrorCS");Q7=makeQuery(id+"F0.imprint","IMPRINT",FACE,{"disambiguationData":[TD([[makeQuery(id+"F0.imprint","IMPRINT",EDGE,{"derivedFrom":subQ0}),-1.0]])]});}
            var Q8;
            {var subQ0=sQuery(id+"F0.wireOp",EDGE,"E76.MirrorCS");Q8=makeQuery(id+"F0.imprint","IMPRINT",FACE,{"disambiguationData":[TD([[makeQuery(id+"F0.imprint","IMPRINT",EDGE,{"derivedFrom":subQ0}),-1.0]])]});}
            var Q9;
            {var subQ0=sQuery(id+"F0.wireOp",EDGE,"E78.MirrorCS");Q9=makeQuery(id+"F0.imprint","IMPRINT",FACE,{"disambiguationData":[TD([[makeQuery(id+"F0.imprint","IMPRINT",EDGE,{"derivedFrom":subQ0}),-1.0]])]});}
            var Q10;
            {var subQ0=sQuery(id+"F0.wireOp",EDGE,"E80.MirrorCS");Q10=makeQuery(id+"F0.imprint","IMPRINT",FACE,{"disambiguationData":[TD([[makeQuery(id+"F0.imprint","IMPRINT",EDGE,{"derivedFrom":subQ0}),1.0]])]});}
            var Q11;
            {var subQ0=sQuery(id+"F0.wireOp",EDGE,"E82.MirrorCS");Q11=makeQuery(id+"F0.imprint","IMPRINT",FACE,{"disambiguationData":[TD([[makeQuery(id+"F0.imprint","IMPRINT",EDGE,{"derivedFrom":subQ0}),-1.0]])]});}
            var Q12;
            {var subQ0=sQuery(id+"F0.wireOp",EDGE,"E41.0");Q12=makeQuery(id+"F0.imprint","IMPRINT",FACE,{"disambiguationData":[TD([[makeQuery(id+"F0.imprint","IMPRINT",EDGE,{"derivedFrom":subQ0}),1.0]])]});}
            var Q13;
            {var subQ0=sQuery(id+"F0.wireOp",EDGE,"E43.0");Q13=makeQuery(id+"F0.imprint","IMPRINT",FACE,{"disambiguationData":[TD([[makeQuery(id+"F0.imprint","IMPRINT",EDGE,{"derivedFrom":subQ0}),1.0]])]});}
            var Q14;
            {var subQ0=sQuery(id+"F0.wireOp",EDGE,"E46.0");Q14=makeQuery(id+"F0.imprint","IMPRINT",FACE,{"disambiguationData":[TD([[makeQuery(id+"F0.imprint","IMPRINT",EDGE,{"derivedFrom":subQ0}),-1.0]])]});}
            var Q15;
            {var subQ0=sQuery(id+"F0.wireOp",EDGE,"E48.MirrorCS");Q15=makeQuery(id+"F0.imprint","IMPRINT",FACE,{"disambiguationData":[TD([[makeQuery(id+"F0.imprint","IMPRINT",EDGE,{"derivedFrom":subQ0}),1.0]])]});}
            var Q16;
            {var subQ0=sQuery(id+"F0.wireOp",EDGE,"E50.MirrorCS");Q16=makeQuery(id+"F0.imprint","IMPRINT",FACE,{"disambiguationData":[TD([[makeQuery(id+"F0.imprint","IMPRINT",EDGE,{"derivedFrom":subQ0}),1.0]])]});}
            var Q17;
            {var subQ0=sQuery(id+"F0.wireOp",EDGE,"E84.MirrorCS");Q17=makeQuery(id+"F0.imprint","IMPRINT",FACE,{"disambiguationData":[TD([[makeQuery(id+"F0.imprint","IMPRINT",EDGE,{"derivedFrom":subQ0}),-1.0]])]});}
            var Q18;
            {var subQ0=sQuery(id+"F0.wireOp",EDGE,"E86.MirrorCS");Q18=makeQuery(id+"F0.imprint","IMPRINT",FACE,{"disambiguationData":[TD([[makeQuery(id+"F0.imprint","IMPRINT",EDGE,{"derivedFrom":subQ0}),-1.0]])]});}
            var Q19;
            {var subQ0=sQuery(id+"F0.wireOp",EDGE,"E92.MirrorCS");Q19=makeQuery(id+"F0.imprint","IMPRINT",FACE,{"disambiguationData":[TD([[makeQuery(id+"F0.imprint","IMPRINT",EDGE,{"derivedFrom":subQ0}),1.0]])]});}
            var Q20;
            {var subQ0=sQuery(id+"F0.wireOp",EDGE,"E90.MirrorCS");Q20=makeQuery(id+"F0.imprint","IMPRINT",FACE,{"disambiguationData":[TD([[makeQuery(id+"F0.imprint","IMPRINT",EDGE,{"derivedFrom":subQ0}),1.0]])]});}
            var Q21;
            {var subQ0=sQuery(id+"F0.wireOp",EDGE,"E60.MirrorCS");Q21=makeQuery(id+"F0.imprint","IMPRINT",FACE,{"disambiguationData":[TD([[makeQuery(id+"F0.imprint","IMPRINT",EDGE,{"derivedFrom":subQ0}),1.0]])]});}
            var Q22;
            {var subQ0=sQuery(id+"F0.wireOp",EDGE,"E58.MirrorCS");Q22=makeQuery(id+"F0.imprint","IMPRINT",FACE,{"disambiguationData":[TD([[makeQuery(id+"F0.imprint","IMPRINT",EDGE,{"derivedFrom":subQ0}),1.0]])]});}
            var Q23;
            {var subQ0=sQuery(id+"F0.wireOp",EDGE,"E62.MirrorCS");Q23=makeQuery(id+"F0.imprint","IMPRINT",FACE,{"disambiguationData":[TD([[makeQuery(id+"F0.imprint","IMPRINT",EDGE,{"derivedFrom":subQ0}),-1.0]])]});}
            var Q24;
            {var subQ4=sQuery(id+"F0.wireOp",EDGE,"E127.MirrorCS");Q24=makeQuery(id+"F0.imprint","IMPRINT",FACE,{"disambiguationData":[TD([[makeQuery(id+"F0.imprint","IMPRINT",EDGE,{"derivedFrom":subQ4}),-1.0]])]});}
            var Q25;
            {var subQ6=sQuery(id+"F0.wireOp",EDGE,"E53.MirrorCS");Q25=makeQuery(id+"F0.imprint","IMPRINT",FACE,{"disambiguationData":[TD([[makeQuery(id+"F0.imprint","IMPRINT",EDGE,{"derivedFrom":subQ6}),-1.0]])]});}
            extrude(context, id + "F3", {"entities" : qUnion([Q0, Q1, Q2, Q3, Q4, Q5, Q6, Q7, Q8, Q9, Q10, Q11, Q12, Q13, Q14, Q15, Q16, Q17, Q18, Q19, Q20, Q21, Q22, Q23, Q24, Q25]), "operationType" : NewBodyOperationType.ADD, "depth" : 52.5 * mm});
        }
        {
            var Q0;
            Q0=makeQuery(id+"F1.opExtrude","CAP_EDGE",EDGE,{"disambiguationData":[OSD([sQuery(id+"F0.wireOp",EDGE,"E24.filletArc")])],"isStart":true});
            fillet(context, id + "F4", {"entities" : qUnion([Q0]), "radius" : 3 * mm, "tangentPropagation" : true, "allowEdgeOverflow" : false});
        }
        {
            var Q0;
            Q0=makeQuery(id+"F1.opExtrude","SWEPT_FACE",FACE,{"disambiguationData":[OSD([sQuery(id+"F0.wireOp",EDGE,"E3.1")])]});
            var sketch = newSketch(context, id + "F5", { "sketchPlane" : qUnion([Q0])});
            skLineSegment(sketch, "E140", {"start": v(-3, 0) * mm, "end": v(-3, 56.5) * mm, "construction": true});
            skLineSegment(sketch, "E141.0", {"start": v(7, 3) * mm, "end": v(7, 56.5) * mm, "construction": true});
            skLineSegment(sketch, "E142.0", {"start": v(33, 3) * mm, "end": v(33, 56.5) * mm, "construction": true});
            skLineSegment(sketch, "E143.bottom", {"start": v(15.26, 12.75) * mm, "end": v(-1.24, 12.75) * mm});
            skLineSegment(sketch, "E143.top", {"start": v(15.26, 46.75) * mm, "end": v(-1.24, 46.75) * mm});
            skLineSegment(sketch, "E143.left", {"start": v(15.26, 12.75) * mm, "end": v(15.26, 46.75) * mm});
            skLineSegment(sketch, "E144", {"start": v(-1.24, 28.25) * mm, "end": v(-3, 28.25) * mm, "construction": true});
            skLineSegment(sketch, "E145.0", {"start": v(53, 0) * mm, "end": v(-59, 0) * mm});
            skLineSegment(sketch, "E146.0", {"start": v(-61.13, -45.2) * mm, "end": v(51.79, -45.2) * mm});
            skLineSegment(sketch, "E147", {"start": v(-29.02, 27) * mm, "end": v(-29.02, 3) * mm, "construction": true});
            skLineSegment(sketch, "E148", {"start": v(-3, 28.25) * mm, "end": v(-57.93, 28.25) * mm, "construction": true});
            skPoint(sketch, "E149", {"position": v(7, 46.75) * mm});
            skLineSegment(sketch, "E150", {"start": v(45, 45.75) * mm, "end": v(45, 13.75) * mm});
            skLineSegment(sketch, "E151", {"start": v(45, 13.75) * mm, "end": v(27, 13.75) * mm});
            skLineSegment(sketch, "E152", {"start": v(27, 13.75) * mm, "end": v(21, 19.75) * mm});
            skLineSegment(sketch, "E153", {"start": v(21, 19.75) * mm, "end": v(21, 39.75) * mm});
            skLineSegment(sketch, "E154", {"start": v(21, 39.75) * mm, "end": v(27, 45.75) * mm});
            skLineSegment(sketch, "E155", {"start": v(27, 45.75) * mm, "end": v(45, 45.75) * mm});
            skLineSegment(sketch, "E156", {"start": v(21, 29.75) * mm, "end": v(45, 29.75) * mm, "construction": true});
            skPoint(sketch, "E157", {"position": v(33, 29.75) * mm});
            skLineSegment(sketch, "E158", {"start": v(33, 29.75) * mm, "end": v(33, 43.5) * mm, "construction": true});
            skCircle(sketch, "E159", {"center": v(33, 49.75) * mm, "radius": 1.35 * mm});
            skCircle(sketch, "E160", {"center": v(33, 9.75) * mm, "radius": 1.35 * mm});
            skLineSegment(sketch, "E161", {"start": v(-1.24, 46.75) * mm, "end": v(-1.24, 12.75) * mm});
            skLineSegment(sketch, "E162", {"start": v(7, 29.75) * mm, "end": v(15.26, 29.75) * mm, "construction": true});
            skSolve(sketch);
        }
        {
            var Q0;
            Q0=makeQuery(id+"F5.imprint","IMPRINT",FACE,{"disambiguationData":[TD([[makeQuery(id+"F5.imprint","IMPRINT",EDGE,{"derivedFrom":sQuery(id+"F5.wireOp",EDGE,"E143.bottom")}),-1.0]])]});
            var Q1;
            Q1=makeQuery(id+"F5.imprint","IMPRINT",FACE,{"disambiguationData":[TD([[makeQuery(id+"F5.imprint","IMPRINT",EDGE,{"derivedFrom":sQuery(id+"F5.wireOp",EDGE,"E150")}),-1.0]])]});
            var Q2;
            Q2=makeQuery(id+"F5.imprint","IMPRINT",FACE,{"disambiguationData":[TD([[makeQuery(id+"F5.imprint","IMPRINT",EDGE,{"derivedFrom":sQuery(id+"F5.wireOp",EDGE,"E160")}),1.0]])]});
            var Q3;
            Q3=makeQuery(id+"F5.imprint","IMPRINT",FACE,{"disambiguationData":[TD([[makeQuery(id+"F5.imprint","IMPRINT",EDGE,{"derivedFrom":sQuery(id+"F5.wireOp",EDGE,"E159")}),1.0]])]});
            extrude(context, id + "F6", {"entities" : qUnion([Q0, Q1, Q2, Q3]), "operationType" : NewBodyOperationType.REMOVE, "oppositeDirection" : true, "depth" : 25 * mm});
        }
        {
            var Q0;
            Q0=makeQuery(id+"F1.opExtrude","SWEPT_FACE",FACE,{"disambiguationData":[OSD([sQuery(id+"F0.wireOp",EDGE,"E3.3")])]});
            var sketch = newSketch(context, id + "F7", { "sketchPlane" : qUnion([Q0])});
            skLineSegment(sketch, "E163", {"start": v(-43.5, 43.75) * mm, "end": v(-43.5, 15.75) * mm});
            skLineSegment(sketch, "E164", {"start": v(-43.5, 15.75) * mm, "end": v(-27, 15.75) * mm});
            skLineSegment(sketch, "E165", {"start": v(-27, 15.75) * mm, "end": v(-23.5, 20.25) * mm});
            skLineSegment(sketch, "E166", {"start": v(-23.5, 20.25) * mm, "end": v(-23.5, 39.25) * mm});
            skLineSegment(sketch, "E167", {"start": v(-23.5, 39.25) * mm, "end": v(-27, 43.75) * mm});
            skLineSegment(sketch, "E168", {"start": v(-27, 43.75) * mm, "end": v(-43.5, 43.75) * mm});
            skLineSegment(sketch, "E169", {"start": v(-53.5, 29.75) * mm, "end": v(-43.5, 29.75) * mm, "construction": true});
            skLineSegment(sketch, "E170", {"start": v(-43.5, 29.75) * mm, "end": v(-23.5, 29.75) * mm, "construction": true});
            skLineSegment(sketch, "E171", {"start": v(-33.5, 51.18) * mm, "end": v(-33.5, 9) * mm, "construction": true});
            skPoint(sketch, "E171.startSnap0", {"position": v(-33.5, 29.75) * mm});
            skCircle(sketch, "E172", {"center": v(-33.5, 49.75) * mm, "radius": 1.35 * mm});
            skCircle(sketch, "E173", {"center": v(-33.5, 9.75) * mm, "radius": 1.35 * mm});
            skSolve(sketch);
        }
        {
            var Q0;
            Q0=makeQuery(id+"F7.imprint","IMPRINT",FACE,{"disambiguationData":[TD([[makeQuery(id+"F7.imprint","IMPRINT",EDGE,{"derivedFrom":sQuery(id+"F7.wireOp",EDGE,"E172")}),1.0]])]});
            var Q1;
            Q1=makeQuery(id+"F7.imprint","IMPRINT",FACE,{"disambiguationData":[TD([[makeQuery(id+"F7.imprint","IMPRINT",EDGE,{"derivedFrom":sQuery(id+"F7.wireOp",EDGE,"E163")}),1.0]])]});
            var Q2;
            Q2=makeQuery(id+"F7.imprint","IMPRINT",FACE,{"disambiguationData":[TD([[makeQuery(id+"F7.imprint","IMPRINT",EDGE,{"derivedFrom":sQuery(id+"F7.wireOp",EDGE,"E173")}),1.0]])]});
            extrude(context, id + "F8", {"entities" : qUnion([Q0, Q1, Q2]), "operationType" : NewBodyOperationType.REMOVE, "oppositeDirection" : true, "depth" : 25 * mm});
        }
        {
            var Q0;
            Q0=makeQuery(id+"F1.opExtrude","SWEPT_BODY",BODY,{"disambiguationData":[OSD([sQuery(id+"F0.wireOp",EDGE,"E0.bottom"),sQuery(id+"F0.wireOp",EDGE,"E0.top"),sQuery(id+"F0.wireOp",EDGE,"E0.left"),sQuery(id+"F0.wireOp",EDGE,"E0.right"),sQuery(id+"F0.wireOp",EDGE,"E1.0"),sQuery(id+"F0.wireOp",EDGE,"E1.1"),sQuery(id+"F0.wireOp",EDGE,"E1.2"),sQuery(id+"F0.wireOp",EDGE,"E1.3"),sQuery(id+"F0.wireOp",EDGE,"E15.filletArc"),sQuery(id+"F0.wireOp",EDGE,"E16.filletArc"),sQuery(id+"F0.wireOp",EDGE,"E17.filletArc"),sQuery(id+"F0.wireOp",EDGE,"E18.filletArc"),sQuery(id+"F0.wireOp",EDGE,"E19.filletArc"),sQuery(id+"F0.wireOp",EDGE,"E20.filletArc"),sQuery(id+"F0.wireOp",EDGE,"E21.filletArc"),sQuery(id+"F0.wireOp",EDGE,"E22.filletArc")])]});
            var Q1;
            {var subQ0=sQuery(id+"F0.wireOp",EDGE,"E3.2");Q1=makeQuery(id+"F4.opFillet","BLEND_EDGE",EDGE,{"blendedFrom":[makeQuery(id+"F1.opExtrude","CAP_EDGE",EDGE,{"disambiguationData":[OSD([subQ0])],"isStart":true}),makeQuery(id+"F1.opExtrude","SWEPT_FACE",FACE,{"disambiguationData":[OSD([subQ0])]})],"blendedInto":[makeQuery(id+"F1.opExtrude","SWEPT_FACE",FACE,{"disambiguationData":[OSD([subQ0])]})]});}
            transform(context, id + "F9", {"entities" : qUnion([Q0]), "transformType" : TransformType.ROTATION, "transformAxis" : qUnion([Q1]), "angle" : 90 * degree, "makeCopy" : false});
        }
        {
            var Q0;
            Q0=makeQuery(id+"F1.opExtrude","SWEPT_FACE",FACE,{"disambiguationData":[OSD([sQuery(id+"F0.wireOp",EDGE,"E3.3")])]});
            var sketch = newSketch(context, id + "F10", { "sketchPlane" : qUnion([Q0])});
            skText(sketch, "E174", { "text": "IN", "fontName": "OpenSans-Bold.ttf"});
            skLineSegment(sketch, "E175", {"start": v(39.74, -87) * mm, "end": v(39.74, -82) * mm, "construction": true});
            const initialGuessF10  = {"E174": [0.03003, -0.082, 1, 0, 0.0125]};
            skSetInitialGuess(sketch, initialGuessF10);
            skSolve(sketch);
        }
        {
            var Q0;
            Q0=makeQuery(id+"F10.imprint","IMPRINT",FACE,{"disambiguationData":[TD([[makeQuery(id+"F10.imprint","IMPRINT",EDGE,{"derivedFrom":sQuery(id+"F10.wireOp",EDGE,"4c00e83c-3f2c-4fb6-bf8e-9947a9ea2a33.sketch_text.stroke-0")}),-1.0]])]});
            var Q1;
            Q1=makeQuery(id+"F10.imprint","IMPRINT",FACE,{"disambiguationData":[TD([[makeQuery(id+"F10.imprint","IMPRINT",EDGE,{"derivedFrom":sQuery(id+"F10.wireOp",EDGE,"4c00e83c-3f2c-4fb6-bf8e-9947a9ea2a33.sketch_text.stroke-14")}),-1.0]])]});
            var Q2;
            Q2=makeQuery(id+"F10.imprint","IMPRINT",FACE,{"disambiguationData":[TD([[makeQuery(id+"F10.imprint","IMPRINT",EDGE,{"derivedFrom":sQuery(id+"F10.wireOp",EDGE,"4c00e83c-3f2c-4fb6-bf8e-9947a9ea2a33.sketch_text.stroke-29")}),-1.0]])]});
            var Q3;
            Q3=makeQuery(id+"F10.imprint","IMPRINT",FACE,{"disambiguationData":[TD([[makeQuery(id+"F10.imprint","IMPRINT",EDGE,{"derivedFrom":sQuery(id+"F10.wireOp",EDGE,"E174.sketch_text.stroke-0")}),-1.0]])]});
            var Q4;
            Q4=makeQuery(id+"F10.imprint","IMPRINT",FACE,{"disambiguationData":[TD([[makeQuery(id+"F10.imprint","IMPRINT",EDGE,{"derivedFrom":sQuery(id+"F10.wireOp",EDGE,"E174.sketch_text.stroke-4")}),-1.0]])]});
            extrude(context, id + "F11", {"entities" : qUnion([Q0, Q1, Q2, Q3, Q4]), "operationType" : NewBodyOperationType.REMOVE, "oppositeDirection" : true, "depth" : 1 * mm});
        }
        {
            var Q0;
            Q0=makeQuery(id+"F1.opExtrude","SWEPT_FACE",FACE,{"disambiguationData":[OSD([sQuery(id+"F0.wireOp",EDGE,"E3.2")])]});
            var sketch = newSketch(context, id + "F12", { "sketchPlane" : qUnion([Q0])});
            skLineSegment(sketch, "E176", {"start": v(39.74, 78.9) * mm, "end": v(39.74, -86.1) * mm, "construction": true});
            skLineSegment(sketch, "E177", {"start": v(66.5, -3.6) * mm, "end": v(13, -3.6) * mm, "construction": true});
            skLineSegment(sketch, "E178.bottom", {"start": v(17, 43.9) * mm, "end": v(62.5, 43.9) * mm});
            skLineSegment(sketch, "E178.top", {"start": v(17, -2.6) * mm, "end": v(62.5, -2.6) * mm});
            skLineSegment(sketch, "E178.left", {"start": v(17, 43.9) * mm, "end": v(17, -2.6) * mm});
            skLineSegment(sketch, "E178.right", {"start": v(62.5, 43.9) * mm, "end": v(62.5, -2.6) * mm});
            skLineSegment(sketch, "E179", {"start": v(39.74, 43.9) * mm, "end": v(39.74, 78.9) * mm, "construction": true});
            skLineSegment(sketch, "E180.bottom", {"start": v(31.5, -12.6) * mm, "end": v(48, -12.6) * mm});
            skLineSegment(sketch, "E180.top", {"start": v(31.5, -47.6) * mm, "end": v(48, -47.6) * mm});
            skLineSegment(sketch, "E180.left", {"start": v(31.5, -12.6) * mm, "end": v(31.5, -47.6) * mm});
            skLineSegment(sketch, "E180.right", {"start": v(48, -12.6) * mm, "end": v(48, -47.6) * mm});
            skLineSegment(sketch, "E181", {"start": v(39.74, -12.6) * mm, "end": v(39.74, -2.6) * mm, "construction": true});
            skText(sketch, "E182", { "text": "OUTPUT", "fontName": "OpenSans-Bold.ttf"});
            skLineSegment(sketch, "E183.0", {"start": v(13, 78.9) * mm, "end": v(66.5, 78.9) * mm});
            skText(sketch, "E184", { "text": "INPUT", "fontName": "OpenSans-Bold.ttf"});
            skText(sketch, "E185", { "text": "PWR", "fontName": "OpenSans-Bold.ttf"});
            const initialGuessF12  = {"E182": [0.01675, 0.0659, 1, 0, 0.008], "E184": [0.02223, -0.0811, 1, 0, 0.008], "E185": [0.02686, -0.0596, 1, 0, 0.008]};
            skSetInitialGuess(sketch, initialGuessF12);
            skSolve(sketch);
        }
        {
            var Q0;
            Q0=makeQuery(id+"F12.imprint","IMPRINT",FACE,{"disambiguationData":[TD([[makeQuery(id+"F12.imprint","IMPRINT",EDGE,{"derivedFrom":sQuery(id+"F12.wireOp",EDGE,"E182.sketch_text.stroke-0")}),-1.0]])]});
            var Q1;
            Q1=makeQuery(id+"F12.imprint","IMPRINT",FACE,{"disambiguationData":[TD([[makeQuery(id+"F12.imprint","IMPRINT",EDGE,{"derivedFrom":sQuery(id+"F12.wireOp",EDGE,"E182.sketch_text.stroke-14")}),-1.0]])]});
            var Q2;
            Q2=makeQuery(id+"F12.imprint","IMPRINT",FACE,{"disambiguationData":[TD([[makeQuery(id+"F12.imprint","IMPRINT",EDGE,{"derivedFrom":sQuery(id+"F12.wireOp",EDGE,"E182.sketch_text.stroke-29")}),-1.0]])]});
            var Q3;
            Q3=makeQuery(id+"F12.imprint","IMPRINT",FACE,{"disambiguationData":[TD([[makeQuery(id+"F12.imprint","IMPRINT",EDGE,{"derivedFrom":sQuery(id+"F12.wireOp",EDGE,"E182.sketch_text.stroke-37")}),-1.0]])]});
            var Q4;
            Q4=makeQuery(id+"F12.imprint","IMPRINT",FACE,{"disambiguationData":[TD([[makeQuery(id+"F12.imprint","IMPRINT",EDGE,{"derivedFrom":sQuery(id+"F12.wireOp",EDGE,"E182.sketch_text.stroke-53")}),-1.0]])]});
            var Q5;
            Q5=makeQuery(id+"F12.imprint","IMPRINT",FACE,{"disambiguationData":[TD([[makeQuery(id+"F12.imprint","IMPRINT",EDGE,{"derivedFrom":sQuery(id+"F12.wireOp",EDGE,"E182.sketch_text.stroke-68")}),-1.0]])]});
            var Q6;
            Q6=makeQuery(id+"F12.imprint","IMPRINT",FACE,{"disambiguationData":[TD([[makeQuery(id+"F12.imprint","IMPRINT",EDGE,{"derivedFrom":sQuery(id+"F12.wireOp",EDGE,"E184.sketch_text.stroke-0")}),-1.0]])]});
            var Q7;
            Q7=makeQuery(id+"F12.imprint","IMPRINT",FACE,{"disambiguationData":[TD([[makeQuery(id+"F12.imprint","IMPRINT",EDGE,{"derivedFrom":sQuery(id+"F12.wireOp",EDGE,"E184.sketch_text.stroke-4")}),-1.0]])]});
            var Q8;
            Q8=makeQuery(id+"F12.imprint","IMPRINT",FACE,{"disambiguationData":[TD([[makeQuery(id+"F12.imprint","IMPRINT",EDGE,{"derivedFrom":sQuery(id+"F12.wireOp",EDGE,"E184.sketch_text.stroke-18")}),-1.0]])]});
            var Q9;
            Q9=makeQuery(id+"F12.imprint","IMPRINT",FACE,{"disambiguationData":[TD([[makeQuery(id+"F12.imprint","IMPRINT",EDGE,{"derivedFrom":sQuery(id+"F12.wireOp",EDGE,"E184.sketch_text.stroke-34")}),-1.0]])]});
            var Q10;
            Q10=makeQuery(id+"F12.imprint","IMPRINT",FACE,{"disambiguationData":[TD([[makeQuery(id+"F12.imprint","IMPRINT",EDGE,{"derivedFrom":sQuery(id+"F12.wireOp",EDGE,"E184.sketch_text.stroke-49")}),-1.0]])]});
            var Q11;
            Q11=makeQuery(id+"F12.imprint","IMPRINT",FACE,{"disambiguationData":[TD([[makeQuery(id+"F12.imprint","IMPRINT",EDGE,{"derivedFrom":sQuery(id+"F12.wireOp",EDGE,"E185.sketch_text.stroke-40")}),-1.0]])]});
            var Q12;
            Q12=makeQuery(id+"F12.imprint","IMPRINT",FACE,{"disambiguationData":[TD([[makeQuery(id+"F12.imprint","IMPRINT",EDGE,{"derivedFrom":sQuery(id+"F12.wireOp",EDGE,"E185.sketch_text.stroke-16")}),-1.0]])]});
            var Q13;
            Q13=makeQuery(id+"F12.imprint","IMPRINT",FACE,{"disambiguationData":[TD([[makeQuery(id+"F12.imprint","IMPRINT",EDGE,{"derivedFrom":sQuery(id+"F12.wireOp",EDGE,"E185.sketch_text.stroke-0")}),-1.0]])]});
            extrude(context, id + "F13", {"entities" : qUnion([Q0, Q1, Q2, Q3, Q4, Q5, Q6, Q7, Q8, Q9, Q10, Q11, Q12, Q13]), "operationType" : NewBodyOperationType.REMOVE, "oppositeDirection" : true, "depth" : 1.2 * mm});
        }
        {
            var Q0;
            Q0=makeQuery(id+"F12.imprint","IMPRINT",FACE,{"disambiguationData":[TD([[makeQuery(id+"F12.imprint","IMPRINT",EDGE,{"derivedFrom":sQuery(id+"F12.wireOp",EDGE,"E178.bottom")}),-1.0]])]});
            var Q1;
            Q1=makeQuery(id+"F12.imprint","IMPRINT",FACE,{"disambiguationData":[TD([[makeQuery(id+"F12.imprint","IMPRINT",EDGE,{"derivedFrom":sQuery(id+"F12.wireOp",EDGE,"E180.bottom")}),-1.0]])]});
            extrude(context, id + "F14", {"entities" : qUnion([Q0, Q1]), "operationType" : NewBodyOperationType.REMOVE, "oppositeDirection" : true, "depth" : 25 * mm});
        }
        {
            var Q0;
            Q0=makeQuery(id+"F1.opExtrude","SWEPT_FACE",FACE,{"disambiguationData":[OSD([sQuery(id+"F0.wireOp",EDGE,"E0.top")])]});
            var sketch = newSketch(context, id + "F15", { "sketchPlane" : qUnion([Q0])});
            skLineSegment(sketch, "E186.bottom", {"start": v(-62.24, -79) * mm, "end": v(-17.24, -79) * mm, "construction": true});
            skLineSegment(sketch, "E186.top", {"start": v(-62.24, -14) * mm, "end": v(-17.24, -14) * mm, "construction": true});
            skLineSegment(sketch, "E186.left", {"start": v(-62.24, -79) * mm, "end": v(-62.24, -14) * mm, "construction": true});
            skLineSegment(sketch, "E186.right", {"start": v(-17.24, -79) * mm, "end": v(-17.24, -14) * mm, "construction": true});
            skLineSegment(sketch, "E187", {"start": v(-39.74, -87) * mm, "end": v(-39.74, -79) * mm, "construction": true});
            skLineSegment(sketch, "E188", {"start": v(-39.74, -79) * mm, "end": v(-39.74, -14) * mm, "construction": true});
            skCircle(sketch, "E189", {"center": v(-39.74, -72) * mm, "radius": 1.8 * mm});
            skCircle(sketch, "E190", {"center": v(-39.74, -21) * mm, "radius": 1.8 * mm});
            skArc(sketch, "E191", {"start": v(-49.74, -18.5) * mm, "mid": v(-52.24, -21) * mm, "end": v(-49.74, -23.5) * mm});
            skArc(sketch, "E192", {"start": v(-29.74, -23.5) * mm, "mid": v(-27.24, -21) * mm, "end": v(-29.74, -18.5) * mm});
            skArc(sketch, "E193", {"start": v(-49.74, -69.5) * mm, "mid": v(-52.24, -72) * mm, "end": v(-49.74, -74.5) * mm});
            skArc(sketch, "E194", {"start": v(-29.74, -74.5) * mm, "mid": v(-27.24, -72) * mm, "end": v(-29.74, -69.5) * mm});
            skLineSegment(sketch, "E195", {"start": v(-29.74, -74.5) * mm, "end": v(-49.74, -74.5) * mm});
            skLineSegment(sketch, "E196", {"start": v(-29.74, -69.5) * mm, "end": v(-49.74, -69.5) * mm});
            skLineSegment(sketch, "E197", {"start": v(-29.74, -23.5) * mm, "end": v(-49.74, -23.5) * mm});
            skLineSegment(sketch, "E198", {"start": v(-29.74, -18.5) * mm, "end": v(-49.74, -18.5) * mm});
            skSolve(sketch);
        }
        {
            var Q0;
            {var subQ0=sQuery(id+"F15.wireOp",EDGE,"E195");Q0=makeQuery(id+"F15.imprint","IMPRINT",FACE,{"disambiguationData":[TD([[makeQuery(id+"F15.imprint","IMPRINT",EDGE,{"derivedFrom":subQ0}),-1.0]])]});}
            var Q1;
            {var subQ0=sQuery(id+"F15.wireOp",EDGE,"E196");Q1=makeQuery(id+"F15.imprint","IMPRINT",FACE,{"disambiguationData":[TD([[makeQuery(id+"F15.imprint","IMPRINT",EDGE,{"derivedFrom":subQ0}),1.0]])]});}
            var Q2;
            Q2=makeQuery(id+"F15.imprint","IMPRINT",FACE,{"disambiguationData":[TD([[makeQuery(id+"F15.imprint","IMPRINT",EDGE,{"derivedFrom":sQuery(id+"F15.wireOp",EDGE,"E190")}),-1.0]])]});
            extrude(context, id + "F16", {"entities" : qUnion([Q0, Q1, Q2]), "operationType" : NewBodyOperationType.ADD, "depth" : 10 * mm});
        }
        {
            var Q0;
            Q0=makeQuery(id+"F1.opExtrude","SWEPT_FACE",FACE,{"disambiguationData":[OSD([sQuery(id+"F0.wireOp",EDGE,"E3.0")])]});
            var sketch = newSketch(context, id + "F17", { "sketchPlane" : qUnion([Q0])});
            skLineSegment(sketch, "E199", {"start": v(39.74, -78.9) * mm, "end": v(39.74, 86.1) * mm, "construction": true});
            skLineSegment(sketch, "E200.0", {"start": v(52.24, -78.9) * mm, "end": v(52.24, 86.1) * mm, "construction": true});
            skLineSegment(sketch, "E201.0", {"start": v(27.24, -78.9) * mm, "end": v(27.24, 86.1) * mm, "construction": true});
            skCircle(sketch, "E202", {"center": v(39.74, -56.4) * mm, "radius": 2.1 * mm});
            skCircle(sketch, "E203", {"center": v(39.74, 3.6) * mm, "radius": 2.1 * mm});
            skCircle(sketch, "E204", {"center": v(39.74, 63.6) * mm, "radius": 2.1 * mm});
            skCircle(sketch, "E205", {"center": v(27.24, 43.6) * mm, "radius": 2.1 * mm});
            skCircle(sketch, "E206", {"center": v(52.24, 43.6) * mm, "radius": 2.1 * mm});
            skCircle(sketch, "E207", {"center": v(27.24, -36.4) * mm, "radius": 2.1 * mm});
            skCircle(sketch, "E208", {"center": v(52.24, -36.4) * mm, "radius": 2.1 * mm});
            skSolve(sketch);
        }
        {
            var Q0;
            Q0=makeQuery(id+"F17.imprint","IMPRINT",FACE,{"disambiguationData":[TD([[makeQuery(id+"F17.imprint","IMPRINT",EDGE,{"derivedFrom":sQuery(id+"F17.wireOp",EDGE,"E202")}),1.0]])]});
            var Q1;
            Q1=makeQuery(id+"F17.imprint","IMPRINT",FACE,{"disambiguationData":[TD([[makeQuery(id+"F17.imprint","IMPRINT",EDGE,{"derivedFrom":sQuery(id+"F17.wireOp",EDGE,"E207")}),1.0]])]});
            var Q2;
            Q2=makeQuery(id+"F17.imprint","IMPRINT",FACE,{"disambiguationData":[TD([[makeQuery(id+"F17.imprint","IMPRINT",EDGE,{"derivedFrom":sQuery(id+"F17.wireOp",EDGE,"E208")}),1.0]])]});
            var Q3;
            Q3=makeQuery(id+"F17.imprint","IMPRINT",FACE,{"disambiguationData":[TD([[makeQuery(id+"F17.imprint","IMPRINT",EDGE,{"derivedFrom":sQuery(id+"F17.wireOp",EDGE,"E203")}),1.0]])]});
            var Q4;
            Q4=makeQuery(id+"F17.imprint","IMPRINT",FACE,{"disambiguationData":[TD([[makeQuery(id+"F17.imprint","IMPRINT",EDGE,{"derivedFrom":sQuery(id+"F17.wireOp",EDGE,"E206")}),1.0]])]});
            var Q5;
            Q5=makeQuery(id+"F17.imprint","IMPRINT",FACE,{"disambiguationData":[TD([[makeQuery(id+"F17.imprint","IMPRINT",EDGE,{"derivedFrom":sQuery(id+"F17.wireOp",EDGE,"E205")}),1.0]])]});
            var Q6;
            Q6=makeQuery(id+"F17.imprint","IMPRINT",FACE,{"disambiguationData":[TD([[makeQuery(id+"F17.imprint","IMPRINT",EDGE,{"derivedFrom":sQuery(id+"F17.wireOp",EDGE,"E204")}),1.0]])]});
            extrude(context, id + "F18", {"entities" : qUnion([Q0, Q1, Q2, Q3, Q4, Q5, Q6]), "operationType" : NewBodyOperationType.REMOVE, "oppositeDirection" : true, "depth" : 25 * mm});
        }
    });
